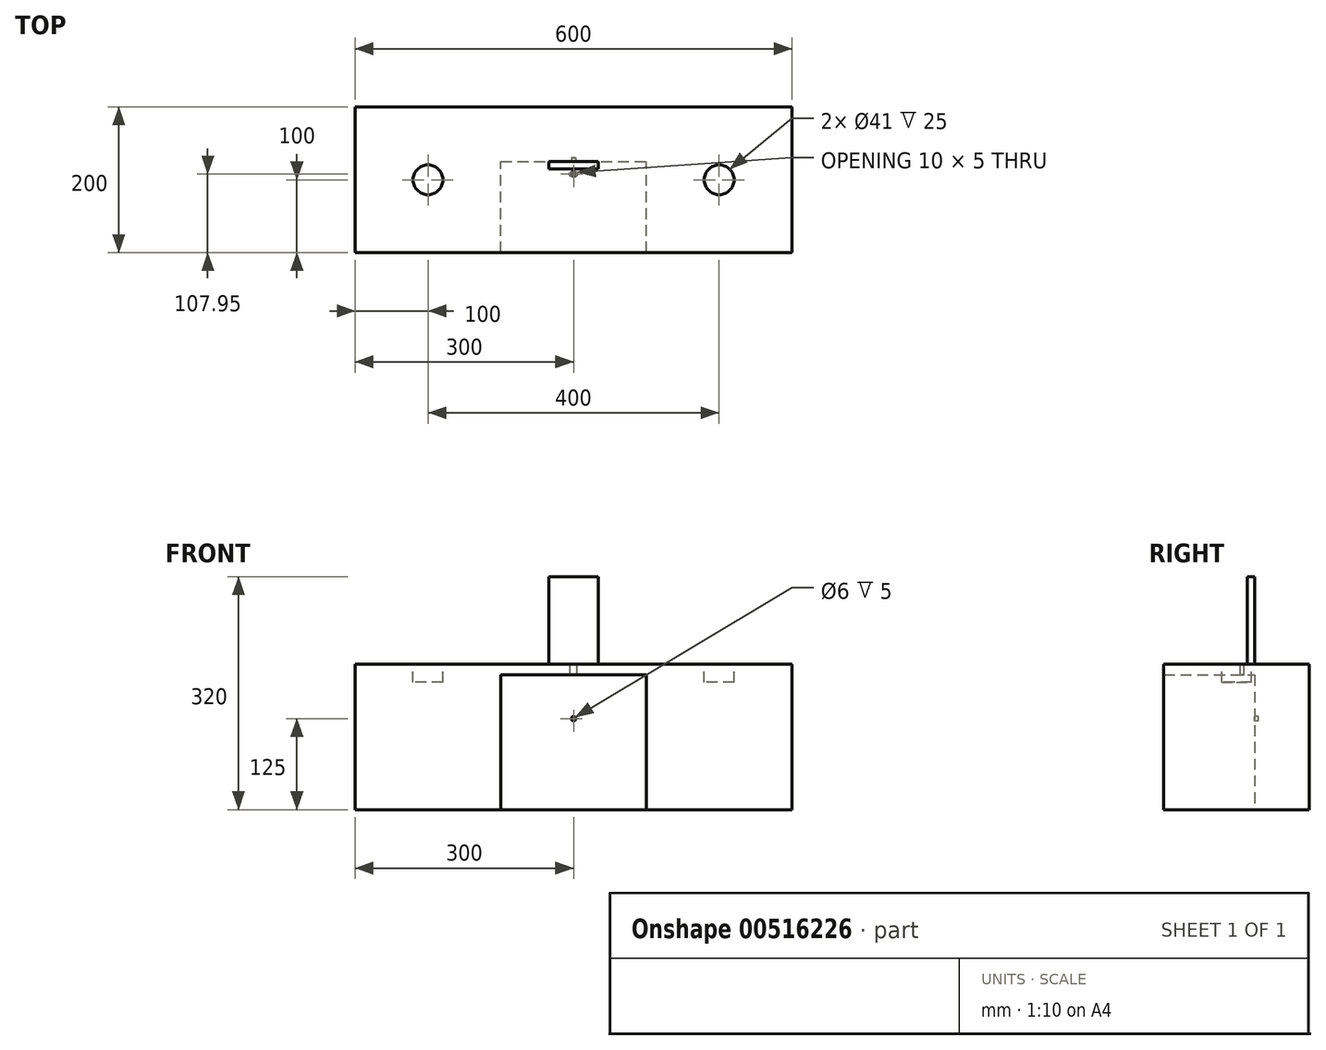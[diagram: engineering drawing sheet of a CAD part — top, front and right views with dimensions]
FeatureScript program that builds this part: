
annotation { "Feature Type Name" : "Feature", "Feature Type Description" : "" }
export const myFeature = defineFeature(function(context is Context, id is Id, definition is map)
    precondition{}
    {
        {
            var Q0;
            Q0=qCreatedBy(makeId("Top.planeOp"),FACE);
            var sketch = newSketch(context, id + "F0", { "sketchPlane" : qUnion([Q0])});
            skLineSegment(sketch, "E0.bottom", {"start": v(-100, 0) * mm, "end": v(-300, 0) * mm});
            skLineSegment(sketch, "E0.top", {"start": v(-100, -200) * mm, "end": v(-300, -200) * mm});
            skLineSegment(sketch, "E0.left", {"start": v(-100, 0) * mm, "end": v(-100, -200) * mm});
            skLineSegment(sketch, "E0.right", {"start": v(-300, 0) * mm, "end": v(-300, -200) * mm});
            skLineSegment(sketch, "E1.bottom", {"start": v(100, 0) * mm, "end": v(300, 0) * mm});
            skLineSegment(sketch, "E1.top", {"start": v(100, -200) * mm, "end": v(300, -200) * mm});
            skLineSegment(sketch, "E1.left", {"start": v(100, 0) * mm, "end": v(100, -200) * mm});
            skLineSegment(sketch, "E1.right", {"start": v(300, 0) * mm, "end": v(300, -200) * mm});
            skLineSegment(sketch, "E2.bottom", {"start": v(-100, 0) * mm, "end": v(100, 0) * mm});
            skLineSegment(sketch, "E2.top", {"start": v(-100, -75) * mm, "end": v(100, -75) * mm});
            skLineSegment(sketch, "E2.left", {"start": v(-100, 0) * mm, "end": v(-100, -75) * mm});
            skLineSegment(sketch, "E2.right", {"start": v(100, 0) * mm, "end": v(100, -75) * mm});
            skSolve(sketch);
        }
        {
            var Q0;
            Q0=makeQuery(id+"F0.imprint","IMPRINT",FACE,{"disambiguationData":[TD([[makeQuery(id+"F0.imprint","IMPRINT",EDGE,{"derivedFrom":sQuery(id+"F0.wireOp",EDGE,"E0.bottom")}),1.0]])]});
            var Q1;
            Q1=makeQuery(id+"F0.imprint","IMPRINT",FACE,{"disambiguationData":[TD([[makeQuery(id+"F0.imprint","IMPRINT",EDGE,{"derivedFrom":sQuery(id+"F0.wireOp",EDGE,"E1.bottom")}),-1.0]])]});
            var Q2;
            Q2=makeQuery(id+"F0.imprint","IMPRINT",FACE,{"disambiguationData":[TD([[makeQuery(id+"F0.imprint","IMPRINT",EDGE,{"derivedFrom":sQuery(id+"F0.wireOp",EDGE,"E2.bottom")}),-1.0]])]});
            extrude(context, id + "F1", {"entities" : qUnion([Q0, Q1, Q2]), "depth" : 200 * mm, "offsetDistance" : 25 * mm});
        }
        {
            var Q0;
            Q0=makeQuery(id+"F1.opExtrude","SWEPT_FACE",FACE,{"disambiguationData":[OSD([sQuery(id+"F0.wireOp",EDGE,"E2.top")])]});
            var sketch = newSketch(context, id + "F2", { "sketchPlane" : qUnion([Q0])});
            skLineSegment(sketch, "E3", {"start": v(-100, 185) * mm, "end": v(100, 185) * mm});
            skSolve(sketch);
        }
        {
            var Q0;
            {var subQ0=sQuery(id+"F2.wireOp",EDGE,"E3");Q0=makeQuery(id+"F2.imprint","IMPRINT",FACE,{"disambiguationData":[TD([[makeQuery(id+"F2.imprint","IMPRINT",EDGE,{"derivedFrom":subQ0}),1.0]])]});}
            extrude(context, id + "F3", {"entities" : qUnion([Q0]), "operationType" : NewBodyOperationType.ADD, "depth" : 125 * mm, "offsetDistance" : 25 * mm});
        }
        {
            var Q0;
            {var subQ0=sQuery(id+"F0.wireOp",EDGE,"E2.top");Q0=makeQuery(id+"F3.boolean.opBoolean","MERGE",FACE,{"derivedFrom":[makeQuery(id+"F1.opExtrude","CAP_FACE",FACE,{"disambiguationData":[OSD([sQuery(id+"F0.wireOp",EDGE,"E0.bottom"),sQuery(id+"F0.wireOp",EDGE,"E0.top"),sQuery(id+"F0.wireOp",EDGE,"E0.left"),sQuery(id+"F0.wireOp",EDGE,"E0.right"),sQuery(id+"F0.wireOp",EDGE,"E1.bottom"),sQuery(id+"F0.wireOp",EDGE,"E1.top"),sQuery(id+"F0.wireOp",EDGE,"E1.left"),sQuery(id+"F0.wireOp",EDGE,"E1.right"),sQuery(id+"F0.wireOp",EDGE,"E2.bottom"),subQ0])],"isStart":false}),makeQuery(id+"F3.opExtrude","SWEPT_FACE",FACE,{"disambiguationData":[OSD([subQ0])]})]});}
            var sketch = newSketch(context, id + "F4", { "sketchPlane" : qUnion([Q0])});
            skLineSegment(sketch, "E4.bottom", {"start": v(-34, -75) * mm, "end": v(34, -75) * mm});
            skLineSegment(sketch, "E4.top", {"start": v(-34, -85) * mm, "end": v(34, -85) * mm});
            skLineSegment(sketch, "E4.left", {"start": v(-34, -75) * mm, "end": v(-34, -85) * mm});
            skLineSegment(sketch, "E4.right", {"start": v(34, -75) * mm, "end": v(34, -85) * mm});
            skSolve(sketch);
        }
        {
            var Q0;
            Q0=makeQuery(id+"F4.imprint","IMPRINT",FACE,{"disambiguationData":[TD([[makeQuery(id+"F4.imprint","IMPRINT",EDGE,{"derivedFrom":sQuery(id+"F4.wireOp",EDGE,"E4.bottom")}),-1.0]])]});
            extrude(context, id + "F5", {"entities" : qUnion([Q0]), "operationType" : NewBodyOperationType.ADD, "depth" : 120 * mm, "offsetDistance" : 25 * mm});
        }
        {
            var Q0;
            {var subQ0=sQuery(id+"F0.wireOp",EDGE,"E2.top");Q0=makeQuery(id+"F3.boolean.opBoolean","MERGE",FACE,{"derivedFrom":[makeQuery(id+"F1.opExtrude","CAP_FACE",FACE,{"disambiguationData":[OSD([sQuery(id+"F0.wireOp",EDGE,"E0.bottom"),sQuery(id+"F0.wireOp",EDGE,"E0.top"),sQuery(id+"F0.wireOp",EDGE,"E0.left"),sQuery(id+"F0.wireOp",EDGE,"E0.right"),sQuery(id+"F0.wireOp",EDGE,"E1.bottom"),sQuery(id+"F0.wireOp",EDGE,"E1.top"),sQuery(id+"F0.wireOp",EDGE,"E1.left"),sQuery(id+"F0.wireOp",EDGE,"E1.right"),sQuery(id+"F0.wireOp",EDGE,"E2.bottom"),subQ0])],"isStart":false}),makeQuery(id+"F3.opExtrude","SWEPT_FACE",FACE,{"disambiguationData":[OSD([subQ0])]})]});}
            var sketch = newSketch(context, id + "F6", { "sketchPlane" : qUnion([Q0])});
            skEllipse(sketch, "E5", {"center": v(0, -92.05) * mm, "majorRadius": 5 * mm, "minorRadius": 2.5 * mm, "majorAxis": v(1, 0)});
            skSolve(sketch);
        }
        {
            var Q0;
            Q0=makeQuery(id+"F6.imprint","IMPRINT",FACE,{"disambiguationData":[TD([[makeQuery(id+"F6.imprint","IMPRINT",EDGE,{"derivedFrom":sQuery(id+"F6.wireOp",EDGE,"E5")}),1.0]])]});
            extrude(context, id + "F7", {"entities" : qUnion([Q0]), "operationType" : NewBodyOperationType.REMOVE, "endBound" : BoundingType.UP_TO_NEXT, "oppositeDirection" : true, "depth" : 25 * mm, "offsetDistance" : 25 * mm});
        }
        {
            var Q0;
            Q0=makeQuery(id+"F1.opExtrude","SWEPT_FACE",FACE,{"disambiguationData":[OSD([sQuery(id+"F0.wireOp",EDGE,"E2.top")])]});
            var sketch = newSketch(context, id + "F8", { "sketchPlane" : qUnion([Q0])});
            skCircle(sketch, "E6", {"center": v(0, 125) * mm, "radius": 3 * mm});
            skSolve(sketch);
        }
        {
            var Q0;
            Q0=makeQuery(id+"F8.imprint","IMPRINT",FACE,{"disambiguationData":[TD([[makeQuery(id+"F8.imprint","IMPRINT",EDGE,{"derivedFrom":sQuery(id+"F8.wireOp",EDGE,"E6")}),1.0]])]});
            extrude(context, id + "F9", {"entities" : qUnion([Q0]), "operationType" : NewBodyOperationType.REMOVE, "oppositeDirection" : true, "depth" : 5 * mm, "offsetDistance" : 25 * mm});
        }
        {
            var Q0;
            {var subQ0=sQuery(id+"F0.wireOp",EDGE,"E2.top");Q0=makeQuery(id+"F3.boolean.opBoolean","MERGE",FACE,{"derivedFrom":[makeQuery(id+"F1.opExtrude","CAP_FACE",FACE,{"disambiguationData":[OSD([sQuery(id+"F0.wireOp",EDGE,"E0.bottom"),sQuery(id+"F0.wireOp",EDGE,"E0.top"),sQuery(id+"F0.wireOp",EDGE,"E0.left"),sQuery(id+"F0.wireOp",EDGE,"E0.right"),sQuery(id+"F0.wireOp",EDGE,"E1.bottom"),sQuery(id+"F0.wireOp",EDGE,"E1.top"),sQuery(id+"F0.wireOp",EDGE,"E1.left"),sQuery(id+"F0.wireOp",EDGE,"E1.right"),sQuery(id+"F0.wireOp",EDGE,"E2.bottom"),subQ0])],"isStart":false}),makeQuery(id+"F3.opExtrude","SWEPT_FACE",FACE,{"disambiguationData":[OSD([subQ0])]})]});}
            var sketch = newSketch(context, id + "F10", { "sketchPlane" : qUnion([Q0])});
            skCircle(sketch, "E7", {"center": v(-200, -100) * mm, "radius": 20.5 * mm});
            skCircle(sketch, "E8", {"center": v(200, -100) * mm, "radius": 20.5 * mm});
            skSolve(sketch);
        }
        {
            var Q0;
            Q0=makeQuery(id+"F10.imprint","IMPRINT",FACE,{"disambiguationData":[TD([[makeQuery(id+"F10.imprint","IMPRINT",EDGE,{"derivedFrom":sQuery(id+"F10.wireOp",EDGE,"E7")}),1.0]])]});
            var Q1;
            Q1=makeQuery(id+"F10.imprint","IMPRINT",FACE,{"disambiguationData":[TD([[makeQuery(id+"F10.imprint","IMPRINT",EDGE,{"derivedFrom":sQuery(id+"F10.wireOp",EDGE,"E8")}),1.0]])]});
            extrude(context, id + "F11", {"entities" : qUnion([Q0, Q1]), "operationType" : NewBodyOperationType.REMOVE, "oppositeDirection" : true, "depth" : 25 * mm, "offsetDistance" : 25 * mm});
        }
    });
